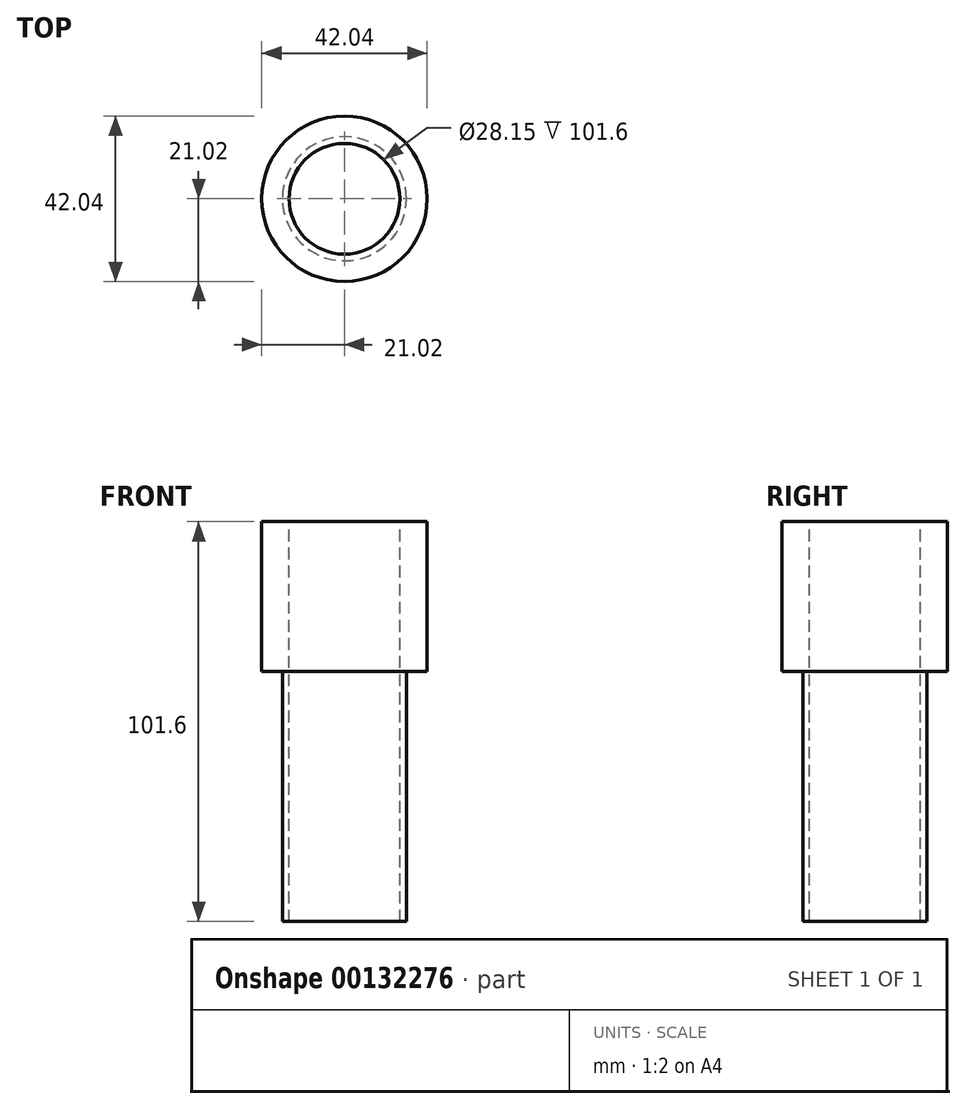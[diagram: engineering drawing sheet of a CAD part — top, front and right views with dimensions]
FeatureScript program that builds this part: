
annotation { "Feature Type Name" : "Feature", "Feature Type Description" : "" }
export const myFeature = defineFeature(function(context is Context, id is Id, definition is map)
    precondition{}
    {
        {
            var Q0;
            Q0=qCreatedBy(makeId("Top.planeOp"),FACE);
            var sketch = newSketch(context, id + "F0", { "sketchPlane" : qUnion([Q0])});
            skCircle(sketch, "E0", {"center": v(0, 0) * mm, "radius": 15.76 * mm});
            skSolve(sketch);
        }
        {
            var Q0;
            Q0 = qSketchRegion(id + "F0", true);
            extrude(context, id + "F1", {"entities" : qUnion([Q0]), "oppositeDirection" : true, "depth" : 101.6 * mm});
        }
        {
            var Q0;
            Q0=qCreatedBy(makeId("Top.planeOp"),FACE);
            var sketch = newSketch(context, id + "F2", { "sketchPlane" : qUnion([Q0])});
            skCircle(sketch, "E1", {"center": v(0, 0) * mm, "radius": 21.02 * mm});
            skSolve(sketch);
        }
        {
            var Q0;
            Q0 = qSketchRegion(id + "F2", true);
            extrude(context, id + "F3", {"entities" : qUnion([Q0]), "operationType" : NewBodyOperationType.ADD, "oppositeDirection" : true, "depth" : 38.1 * mm});
        }
        {
            var Q0;
            Q0=makeQuery(id+"F3.boolean.opBoolean","MERGE",FACE,{"derivedFrom":[makeQuery(id+"F1.opExtrude","CAP_FACE",FACE,{"disambiguationData":[OSD([sQuery(id+"F0.wireOp",EDGE,"E0")])],"isStart":true}),makeQuery(id+"F3.opExtrude","CAP_FACE",FACE,{"disambiguationData":[OSD([sQuery(id+"F2.wireOp",EDGE,"E1")])],"isStart":true})]});
            var sketch = newSketch(context, id + "F4", { "sketchPlane" : qUnion([Q0])});
            skCircle(sketch, "E2", {"center": v(0, 0) * mm, "radius": 14.07 * mm});
            skSolve(sketch);
        }
        {
            var Q0;
            Q0 = qSketchRegion(id + "F4", true);
            extrude(context, id + "F5", {"entities" : qUnion([Q0]), "operationType" : NewBodyOperationType.REMOVE, "endBound" : BoundingType.THROUGH_ALL, "oppositeDirection" : true, "depth" : 25.4 * mm});
        }
    });
